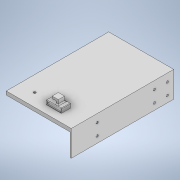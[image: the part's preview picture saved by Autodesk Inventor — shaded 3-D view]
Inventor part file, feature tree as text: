
AUTODESK INVENTOR PART (.ipt)
format: ipt  version: 2021 (Build 250183000, 183)  size: 238,592 bytes
history: native  units: mm
features: sketch x6, extrude x4, other x3, projected_geometry x3, hole x2
ambient origin geometry x8: Origin, YZ Plane, XZ Plane, XY Plane, X Axis, Y Axis, Z Axis, Center Point
bodies: Solid1 (feature_tree)
feature tree (18):
  other  "wallMount.ipt"
  extrude  "Extrusion3"  Depth=10.0mm
  hole  "Hole2"  [1 undecoded]
  extrude  "Extrusion4"  Depth=124.75mm TaperAngle=0.0deg
  extrude  "Extrusion5"  TaperAngle=0.0deg  [1 undecoded]
  hole  "Hole3"  [1 undecoded]
  extrude  "Extrusion6"  [1 undecoded]
  other  "Solid2::wallMount.ipt"
  other  "TaggingFeature1"
  sketch  "Sketch4"  dims[d0=10.0mm d15=25.0mm]
  projected_geometry  "Projected Loop3"
  projected_geometry  "Projected Loop4"
  sketch  "Sketch5"  dims[d16=124.75mm d17=0.0mm]
  projected_geometry  "Projected Loop5"
  sketch  "Sketch6"  dims[d18=4.5mm d19=6.0mm d20=7.5mm d21=2.0mm d22=90.0deg d23=8.0mm d24=20.594885mm d25=25.0mm]
  sketch  "Sketch7"  dims[d26=124.75mm d27=0.0mm d28=124.75mm d29=0.0mm]
  sketch  "Sketch8"  dims[d30=4.5mm d31=6.0mm d32=7.5mm d33=2.0mm d34=90.0deg d35=8.0mm d36=20.594885mm d37=0.0mm d38=0.0mm]
  sketch  "Sketch9"  dims[d39=60.0mm]
note: 4 required parameter values undecoded (feature->parameter linkage not recoverable at this tier; creation-order binding heuristic only, values carry confidence <= 0.55)
